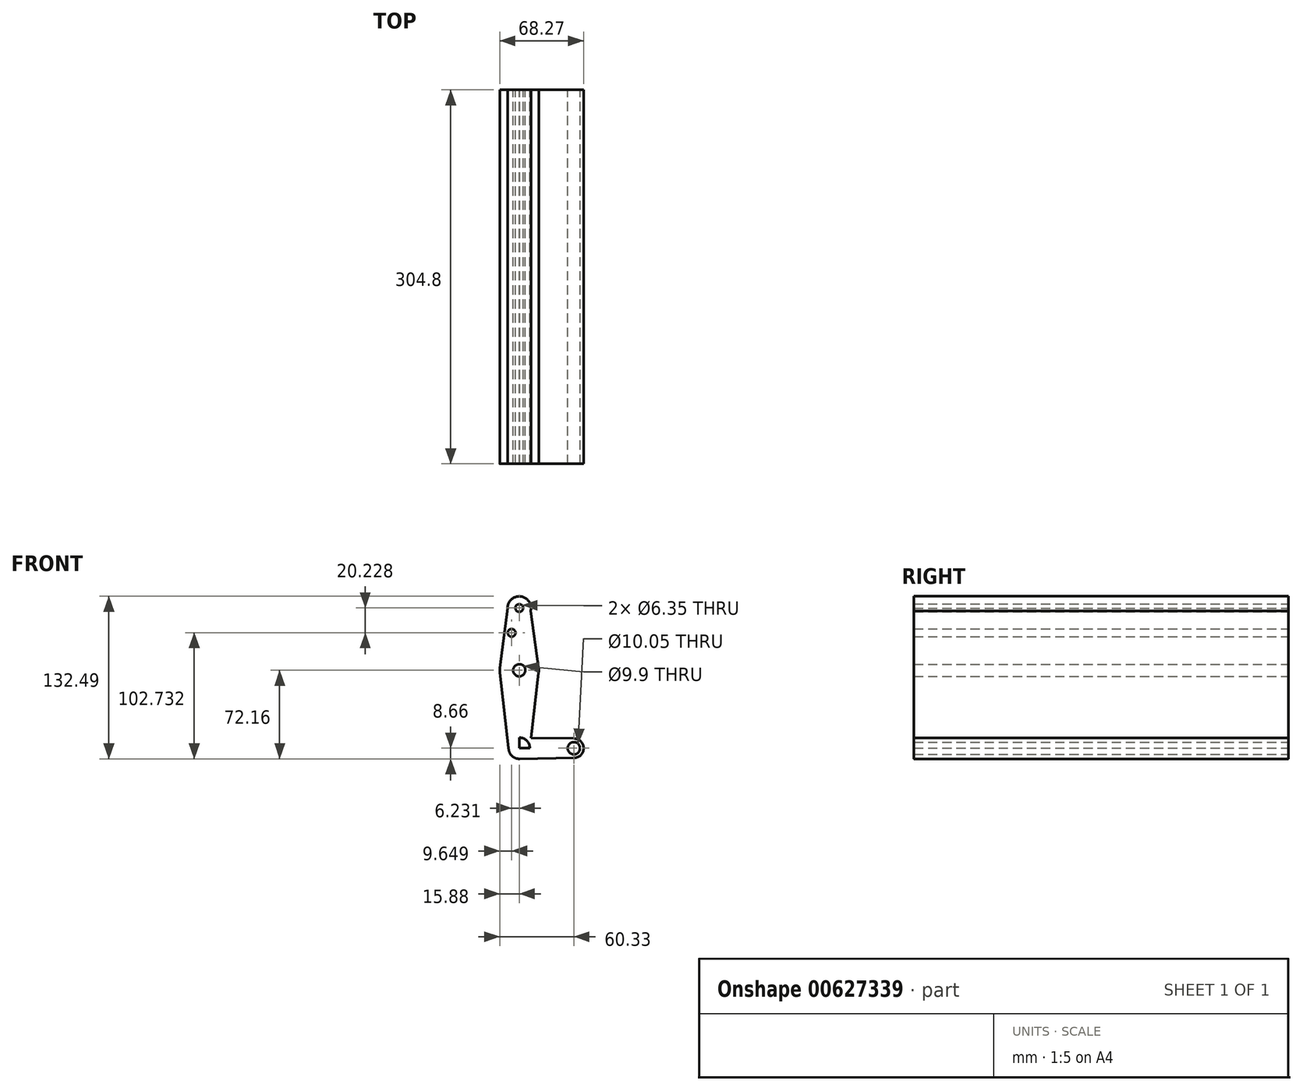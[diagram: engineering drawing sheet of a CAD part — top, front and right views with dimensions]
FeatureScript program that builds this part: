
annotation { "Feature Type Name" : "Feature", "Feature Type Description" : "" }
export const myFeature = defineFeature(function(context is Context, id is Id, definition is map)
    precondition{}
    {
        {
            var Q0;
            Q0=qCreatedBy(makeId("Front.planeOp"),FACE);
            var sketch = newSketch(context, id + "F0", { "sketchPlane" : qUnion([Q0])});
            skLineSegment(sketch, "E0", {"start": v(0, 114.3) * mm, "end": v(0, 0) * mm});
            skLineSegment(sketch, "E1", {"start": v(0, 0) * mm, "end": v(44.45, 0) * mm});
            skCircle(sketch, "E2", {"center": v(0, 114.3) * mm, "radius": 9.53 * mm});
            skCircle(sketch, "E3", {"center": v(0, 63.5) * mm, "radius": 15.88 * mm});
            skCircle(sketch, "E4", {"center": v(0, 0) * mm, "radius": 8.66 * mm});
            skCircle(sketch, "E5", {"center": v(44.45, 0) * mm, "radius": 7.94 * mm});
            skLineSegment(sketch, "E6", {"start": v(-9.52, 114.04) * mm, "end": v(-15.75, 65.52) * mm});
            skLineSegment(sketch, "E7", {"start": v(-8.66, 0) * mm, "end": v(-15.77, 61.68) * mm});
            skLineSegment(sketch, "E8", {"start": v(9.21, 111.89) * mm, "end": v(15.72, 65.71) * mm});
            skLineSegment(sketch, "E9", {"start": v(15.75, 61.54) * mm, "end": v(8.66, 0) * mm});
            skLineSegment(sketch, "E10", {"start": v(0, 8.66) * mm, "end": v(44.58, 7.94) * mm});
            skLineSegment(sketch, "E11", {"start": v(0, -8.66) * mm, "end": v(44.58, -7.94) * mm});
            skCircle(sketch, "E12", {"center": v(0, 114.3) * mm, "radius": 3.18 * mm});
            skCircle(sketch, "E13", {"center": v(-6.23, 94.07) * mm, "radius": 3.18 * mm});
            skCircle(sketch, "E14", {"center": v(0, 63.5) * mm, "radius": 4.95 * mm});
            skCircle(sketch, "E15", {"center": v(44.45, 0) * mm, "radius": 5.02 * mm});
            skSolve(sketch);
        }
        {
            var Q0;
            Q0 = qSketchRegion(id + "F0", true);
            extrude(context, id + "F1", {"entities" : qUnion([Q0]), "depth" : 304.8 * mm, "offsetDistance" : 25.4 * mm});
        }
    });
